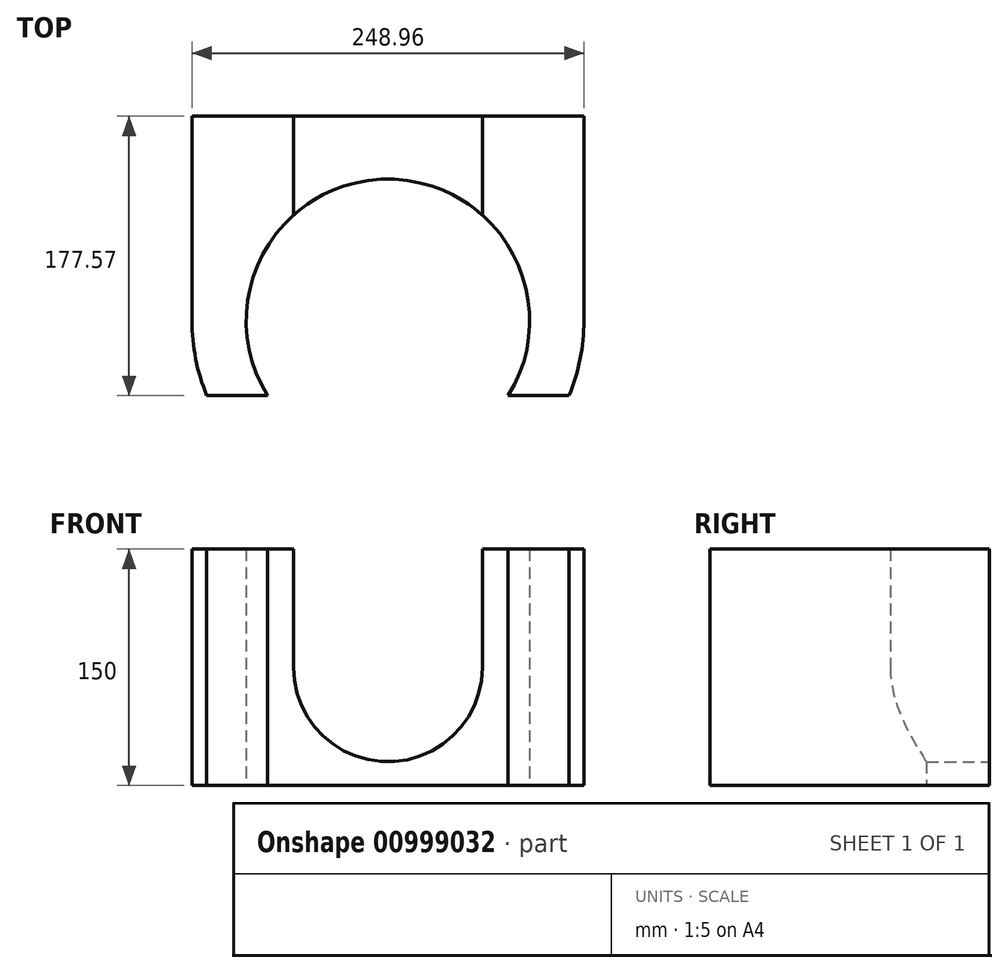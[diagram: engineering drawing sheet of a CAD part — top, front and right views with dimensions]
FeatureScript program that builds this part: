
annotation { "Feature Type Name" : "Feature", "Feature Type Description" : "" }
export const myFeature = defineFeature(function(context is Context, id is Id, definition is map)
    precondition{}
    {
        {
            var Q0;
            Q0=qCreatedBy(makeId("Top.planeOp"),FACE);
            var sketch = newSketch(context, id + "F0", { "sketchPlane" : qUnion([Q0])});
            skArc(sketch, "E0", {"start": v(76.4, -47.57) * mm, "mid": v(0, 90) * mm, "end": v(-76.4, -47.57) * mm});
            skArc(sketch, "E1", {"start": v(115.04, -47.57) * mm, "mid": v(122.1, -24.25) * mm, "end": v(124.48, 0) * mm});
            skLineSegment(sketch, "E2.top", {"start": v(-124.48, 130) * mm, "end": v(124.48, 130) * mm});
            skLineSegment(sketch, "E2.left", {"start": v(-124.48, 0) * mm, "end": v(-124.48, 130) * mm});
            skLineSegment(sketch, "E2.right", {"start": v(124.48, 0) * mm, "end": v(124.48, 130) * mm});
            skPoint(sketch, "E2.middle", {"position": v(0, 95.23) * mm});
            skLineSegment(sketch, "E3.bottom", {"start": v(-115.04, -47.57) * mm, "end": v(-76.4, -47.57) * mm});
            skLineSegment(sketch, "E4.trimOffspring", {"start": v(76.4, -47.57) * mm, "end": v(115.04, -47.57) * mm});
            skArc(sketch, "E5.trimOffspring", {"start": v(-124.48, 0) * mm, "mid": v(-122.1, -24.25) * mm, "end": v(-115.04, -47.57) * mm});
            skSolve(sketch);
        }
        {
            var Q0;
            Q0 = qSketchRegion(id + "F0", true);
            extrude(context, id + "F1", {"entities" : qUnion([Q0]), "depth" : 150 * mm, "offsetDistance" : 25.4 * mm});
        }
        {
            var Q0;
            Q0=makeQuery(id+"F1.opExtrude","SWEPT_FACE",FACE,{"disambiguationData":[OSD([sQuery(id+"F0.wireOp",EDGE,"E2.top")])]});
            var sketch = newSketch(context, id + "F2", { "sketchPlane" : qUnion([Q0])});
            skLineSegment(sketch, "E6", {"start": v(0, 0) * mm, "end": v(0, 150) * mm, "construction": true});
            skArc(sketch, "E7", {"start": v(-60, 75) * mm, "mid": v(0, 15) * mm, "end": v(60, 75) * mm});
            skLineSegment(sketch, "E8", {"start": v(-60, 150) * mm, "end": v(-60, 75) * mm});
            skLineSegment(sketch, "E9.MirrorCS", {"start": v(60, 150) * mm, "end": v(60, 75) * mm});
            skLineSegment(sketch, "E10", {"start": v(-60, 150) * mm, "end": v(60, 150) * mm});
            skSolve(sketch);
        }
        {
            var Q0;
            Q0 = qSketchRegion(id + "F2", true);
            extrude(context, id + "F3", {"entities" : qUnion([Q0]), "operationType" : NewBodyOperationType.REMOVE, "oppositeDirection" : true, "depth" : 152.65 * mm, "offsetDistance" : 25.4 * mm});
        }
    });
